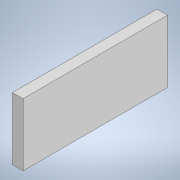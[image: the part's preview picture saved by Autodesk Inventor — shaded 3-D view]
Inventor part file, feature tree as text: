
AUTODESK INVENTOR PART (.ipt)
format: ipt  version: 2020 (Build 240168000, 168)  size: 87,040 bytes
history: native  units: mm
features: extrude x1, sketch x1
ambient origin geometry x8: Origin, YZ Plane, XZ Plane, XY Plane, X Axis, Y Axis, Z Axis, Center Point
bodies: Solide1 (feature_tree)
feature tree (2):
  extrude  "Extrusion1"  Depth=22.0mm
  sketch  "Esquisse1"
